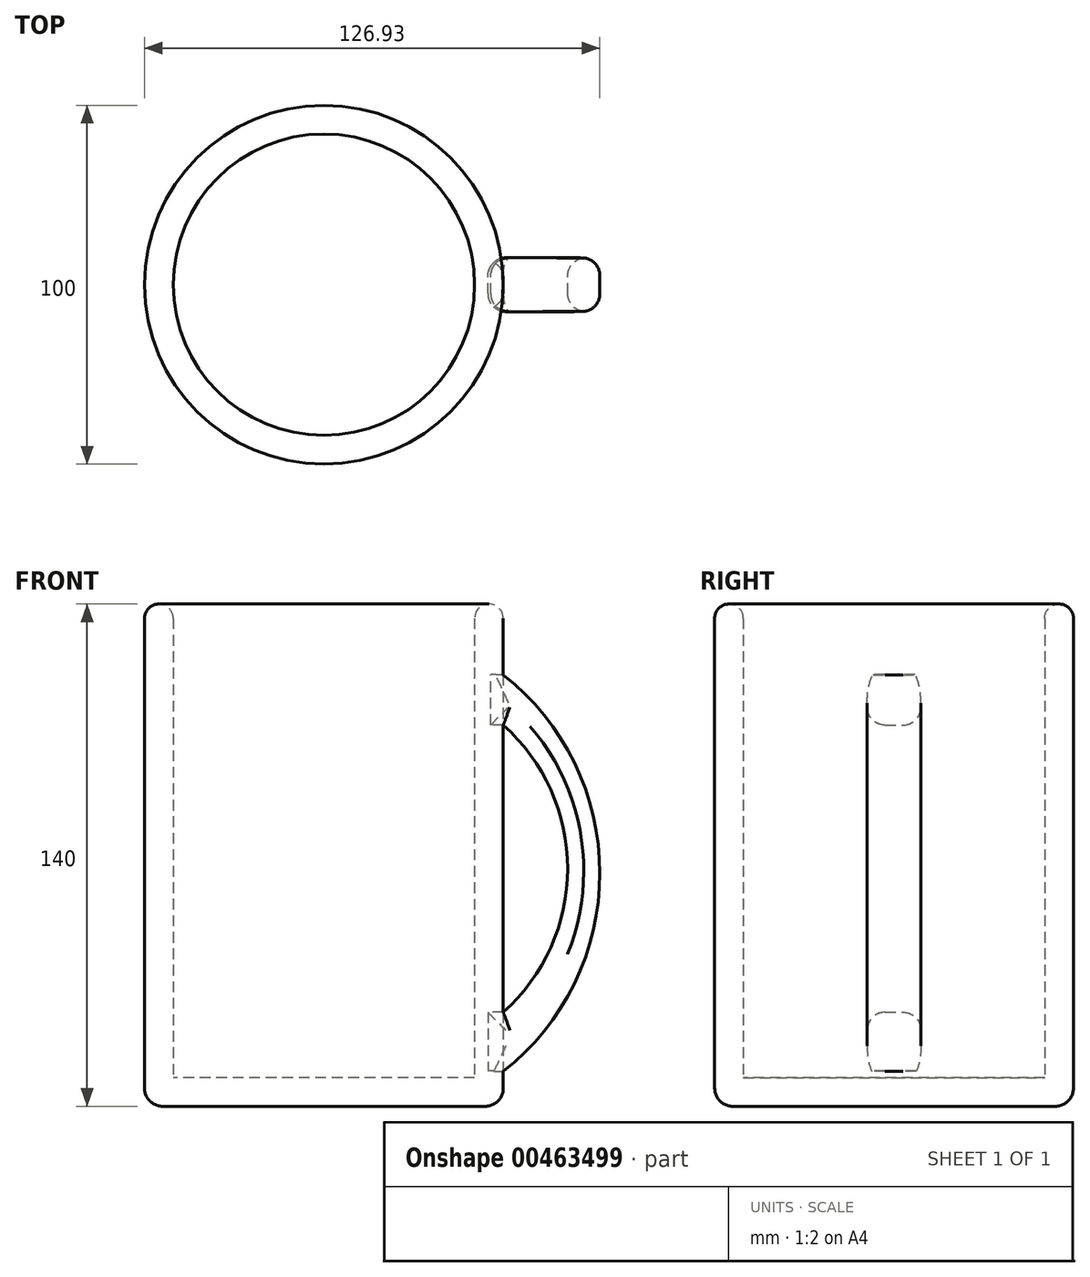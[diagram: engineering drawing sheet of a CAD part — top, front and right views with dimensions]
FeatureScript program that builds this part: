
annotation { "Feature Type Name" : "Feature", "Feature Type Description" : "" }
export const myFeature = defineFeature(function(context is Context, id is Id, definition is map)
    precondition{}
    {
        {
            var Q0;
            Q0=qCreatedBy(makeId("Top.planeOp"),FACE);
            var sketch = newSketch(context, id + "F0", { "sketchPlane" : qUnion([Q0])});
            skCircle(sketch, "E0", {"center": v(0, 0) * mm, "radius": 50 * mm});
            skSolve(sketch);
        }
        {
            var Q0;
            Q0 = qSketchRegion(id + "F0", true);
            extrude(context, id + "F1", {"entities" : qUnion([Q0]), "depth" : 140 * mm});
        }
        {
            var Q0;
            Q0=makeQuery(id+"F1.opExtrude","CAP_FACE",FACE,{"disambiguationData":[OSD([sQuery(id+"F0.wireOp",EDGE,"E0")])],"isStart":false});
            shell(context, id + "F2", {"entities" : qUnion([Q0]), "thickness" : 8 * mm});
        }
        {
            var Q0;
            Q0=makeQuery(id+"F1.opExtrude","CAP_EDGE",EDGE,{"disambiguationData":[OSD([sQuery(id+"F0.wireOp",EDGE,"E0")])],"isStart":false});
            var Q1;
            {var subQ0=sQuery(id+"F0.wireOp",EDGE,"E0");Q1=makeQuery(id+"F2.opShell","OFFSET_EDGE",EDGE,{"disambiguationData":[OSD([subQ0]),TDD([makeQuery(id+"F1.opExtrude","CAP_EDGE",EDGE,{"disambiguationData":[OSD([subQ0])],"isStart":false})])]});}
            fillet(context, id + "F3", {"entities" : qUnion([Q0, Q1]), "radius" : 4 * mm, "tangentPropagation" : true, "allowEdgeOverflow" : false});
        }
        {
            var Q0;
            Q0=qCreatedBy(makeId("Front.planeOp"),FACE);
            var sketch = newSketch(context, id + "F4", { "sketchPlane" : qUnion([Q0])});
            skLineSegment(sketch, "E1", {"start": v(0, 0) * mm, "end": v(50, 0) * mm});
            skLineSegment(sketch, "E2", {"start": v(50, 0) * mm, "end": v(50, 9.7) * mm});
            skPoint(sketch, "E3.4.internal.snap0", {"position": v(50, 66.8) * mm});
            skArc(sketch, "E4", {"start": v(50, 26.22) * mm, "mid": v(67.96, 66.24) * mm, "end": v(50, 106.25) * mm});
            skArc(sketch, "E5", {"start": v(50, 9.7) * mm, "mid": v(76.93, 64.98) * mm, "end": v(50, 120.25) * mm});
            skLineSegment(sketch, "E6", {"start": v(50, 26.22) * mm, "end": v(45.7, 26.22) * mm});
            skLineSegment(sketch, "E7", {"start": v(45.7, 26.22) * mm, "end": v(45.7, 9.84) * mm});
            skLineSegment(sketch, "E8", {"start": v(45.7, 9.84) * mm, "end": v(50, 9.7) * mm});
            skLineSegment(sketch, "E9", {"start": v(50, 106.25) * mm, "end": v(46.5, 106.25) * mm});
            skLineSegment(sketch, "E10", {"start": v(46.5, 106.25) * mm, "end": v(46.5, 120.3) * mm});
            skLineSegment(sketch, "E11", {"start": v(46.5, 120.3) * mm, "end": v(50, 120.25) * mm});
            skLineSegment(sketch, "E12.trimOffspring", {"start": v(50, 120.25) * mm, "end": v(50, 133.6) * mm});
            skLineSegment(sketch, "E13.trimOffspring", {"start": v(50, 26.22) * mm, "end": v(50, 106.25) * mm});
            skSolve(sketch);
        }
        {
            var Q0;
            Q0=makeQuery(id+"F4.imprint","IMPRINT",FACE,{"disambiguationData":[TD([[makeQuery(id+"F4.imprint","IMPRINT",EDGE,{"derivedFrom":sQuery(id+"F4.wireOp",EDGE,"E4")}),-1.0]])]});
            extrude(context, id + "F5", {"entities" : qUnion([Q0]), "endBound" : BoundingType.SYMMETRIC, "depth" : 15 * mm});
        }
        {
            var Q0;
            Q0=makeQuery(id+"F1.opExtrude","CAP_EDGE",EDGE,{"disambiguationData":[OSD([sQuery(id+"F0.wireOp",EDGE,"E0")])],"isStart":true});
            fillet(context, id + "F6", {"entities" : qUnion([Q0]), "radius" : 5 * mm, "tangentPropagation" : true, "allowEdgeOverflow" : false});
        }
        {
            var Q0;
            Q0=makeQuery(id+"F5.opExtrude","CAP_EDGE",EDGE,{"disambiguationData":[OSD([sQuery(id+"F4.wireOp",EDGE,"E5")])],"isStart":false});
            var Q1;
            Q1=makeQuery(id+"F5.opExtrude","CAP_EDGE",EDGE,{"disambiguationData":[OSD([sQuery(id+"F4.wireOp",EDGE,"E5")])],"isStart":true});
            var Q2;
            Q2=makeQuery(id+"F5.opExtrude","CAP_EDGE",EDGE,{"disambiguationData":[OSD([sQuery(id+"F4.wireOp",EDGE,"E4")])],"isStart":false});
            var Q3;
            Q3=makeQuery(id+"F5.opExtrude","CAP_EDGE",EDGE,{"disambiguationData":[OSD([sQuery(id+"F4.wireOp",EDGE,"E4")])],"isStart":true});
            var Q4;
            Q4=makeQuery(id+"F5.opExtrude","CAP_FACE",FACE,{"disambiguationData":[OSD([sQuery(id+"F4.wireOp",EDGE,"E4"),sQuery(id+"F4.wireOp",EDGE,"E5"),sQuery(id+"F4.wireOp",EDGE,"E6"),sQuery(id+"F4.wireOp",EDGE,"E7"),sQuery(id+"F4.wireOp",EDGE,"E8"),sQuery(id+"F4.wireOp",EDGE,"E9"),sQuery(id+"F4.wireOp",EDGE,"E10"),sQuery(id+"F4.wireOp",EDGE,"E11")])],"isStart":true});
            var Q5;
            Q5=makeQuery(id+"F5.opExtrude","CAP_FACE",FACE,{"disambiguationData":[OSD([sQuery(id+"F4.wireOp",EDGE,"E4"),sQuery(id+"F4.wireOp",EDGE,"E5"),sQuery(id+"F4.wireOp",EDGE,"E6"),sQuery(id+"F4.wireOp",EDGE,"E7"),sQuery(id+"F4.wireOp",EDGE,"E8"),sQuery(id+"F4.wireOp",EDGE,"E9"),sQuery(id+"F4.wireOp",EDGE,"E10"),sQuery(id+"F4.wireOp",EDGE,"E11")])],"isStart":false});
            fillet(context, id + "F7", {"entities" : qUnion([Q0, Q1, Q2, Q3, Q4, Q5]), "radius" : 5 * mm, "tangentPropagation" : true, "allowEdgeOverflow" : false});
        }
    });
